# Revit family: Dropp ks 104
name_source: partatom
category: Мебель
revit_build: Autodesk Revit 2017 (Build: 20160225_1515(x64)
units: mm (PartAtom-declared; Revit-internal decimal feet)

## family parameters
Всегда вертикально = Да
Заголовок OmniClass = General Furniture and Specialties
На основе рабочей плоскости = Нет
Номер OmniClass = 23.40.20.00
Общий = Нет
При загрузке вырезать с полостями = Нет
Точка расчета площади = Нет

## types (6) — shared parameters
Leg = Skandiform Chrome
Seat = Skandiform Fabric
Изготовитель = Skandiform AB
Комментарии к типоразмеру = Created by Astacus AB
Описание = Chassis in chromium or silver lacquered metal

## per-type parameters (varying)
| type | Type | URL | Ключевая пометка |
| F-202 | F-202 | http://www.biminfo.se | XBF.3 |
| F-201 | F-201 | http://www.biminfo.se | XBF.3 |
| FP-022 | FP-022 | http://www.biminfo.se | XBF.3 |
| KS-104 | KS-104 | http://www.biminfo.se | XBF.4 |
| SA-203 | SA-203 | http://www.biminfo.se | XBF.4 |
| S-022 | KS-104 | http://file-system.ru | XBF.3 |

note: column(s) folded — value = type name in every type: Группа модели

## geometry (parser evidence)
native form markers: Blend x3, Sweep x20
no freeform markers — native parametric forms only
